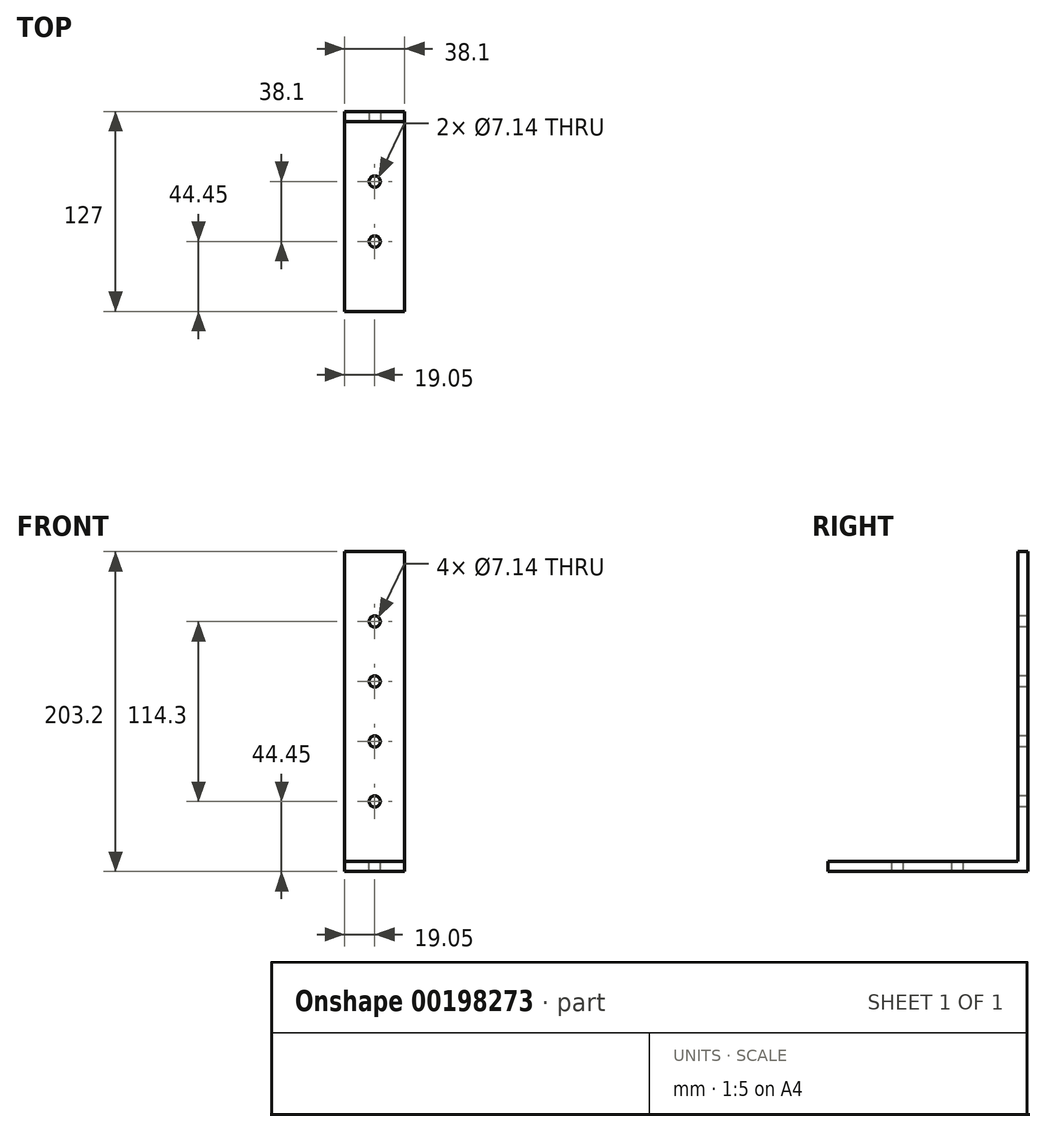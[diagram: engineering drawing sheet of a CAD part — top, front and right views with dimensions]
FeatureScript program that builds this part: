
annotation { "Feature Type Name" : "Feature", "Feature Type Description" : "" }
export const myFeature = defineFeature(function(context is Context, id is Id, definition is map)
    precondition{}
    {
        {
            var Q0;
            Q0=qCreatedBy(makeId("Right.planeOp"),FACE);
            var sketch = newSketch(context, id + "F0", { "sketchPlane" : qUnion([Q0])});
            skLineSegment(sketch, "E0", {"start": v(0, 203.2) * mm, "end": v(0, 0) * mm});
            skLineSegment(sketch, "E1", {"start": v(0, 0) * mm, "end": v(-127, 0) * mm});
            skLineSegment(sketch, "E2.0", {"start": v(-6.35, 6.35) * mm, "end": v(-127, 6.35) * mm});
            skLineSegment(sketch, "E2.1", {"start": v(-6.35, 203.2) * mm, "end": v(-6.35, 6.35) * mm});
            skLineSegment(sketch, "E3", {"start": v(-127, 6.35) * mm, "end": v(-127, 0) * mm});
            skLineSegment(sketch, "E4", {"start": v(-6.35, 203.2) * mm, "end": v(0, 203.2) * mm});
            skSolve(sketch);
        }
        {
            var Q0;
            Q0 = qSketchRegion(id + "F0", true);
            extrude(context, id + "F1", {"entities" : qUnion([Q0]), "endBound" : BoundingType.SYMMETRIC, "depth" : 38.1 * mm, "offsetDistance" : 25.4 * mm});
        }
        {
            var Q0;
            Q0=makeQuery(id+"F1.opExtrude","SWEPT_FACE",FACE,{"disambiguationData":[OSD([sQuery(id+"F0.wireOp",EDGE,"E2.0")])]});
            var sketch = newSketch(context, id + "F2", { "sketchPlane" : qUnion([Q0])});
            skPoint(sketch, "E5", {"position": v(0, -82.55) * mm});
            skPoint(sketch, "E6", {"position": v(0, -44.45) * mm});
            skSolve(sketch);
        }
        {
            var Q0;
            Q0=makeQuery(id+"F1.opExtrude","SWEPT_FACE",FACE,{"disambiguationData":[OSD([sQuery(id+"F0.wireOp",EDGE,"E2.1")])]});
            var sketch = newSketch(context, id + "F3", { "sketchPlane" : qUnion([Q0])});
            skPoint(sketch, "E7", {"position": v(0, 44.45) * mm});
            skPoint(sketch, "E8.0.1.0", {"position": v(0, 82.55) * mm});
            skPoint(sketch, "E8.0.2.0", {"position": v(0, 120.65) * mm});
            skPoint(sketch, "E8.0.3.0", {"position": v(0, 158.75) * mm});
            skLineSegment(sketch, "E8.direction1", {"start": v(0, 44.45) * mm, "end": v(25.4, 44.45) * mm, "construction": true});
            skLineSegment(sketch, "E8.direction2", {"start": v(0, 44.45) * mm, "end": v(0, 82.55) * mm, "construction": true});
            skSolve(sketch);
        }
        {
            var Q0;
            Q0=sQuery(id+"F3.wireOp",VERTEX,"E8.0.3.0");
            var Q1;
            Q1=sQuery(id+"F3.wireOp",VERTEX,"E8.0.2.0");
            var Q2;
            Q2=sQuery(id+"F3.wireOp",VERTEX,"E8.0.1.0");
            var Q3;
            Q3=sQuery(id+"F3.wireOp",VERTEX,"E8.direction1.start");
            var Q4;
            Q4=sQuery(id+"F2.wireOp",VERTEX,"E6");
            var Q5;
            Q5=sQuery(id+"F2.wireOp",VERTEX,"E5");
            var Q6;
            Q6=makeQuery(id+"F1.opExtrude","SWEPT_BODY",BODY,{"disambiguationData":[OSD([sQuery(id+"F0.wireOp",EDGE,"E0"),sQuery(id+"F0.wireOp",EDGE,"E1"),sQuery(id+"F0.wireOp",EDGE,"E2.0"),sQuery(id+"F0.wireOp",EDGE,"E2.1"),sQuery(id+"F0.wireOp",EDGE,"E3"),sQuery(id+"F0.wireOp",EDGE,"E4")])]});
            hole(context, id + "F4", {"style" : HoleStyle.SIMPLE, "endStyle" : HoleEndStyle.THROUGH, "standardTappedOrClearance" : lookupTablePath({ "standard" : "ANSI", "fit" : "Normal (ASME)", "size" : "1/4", "type" : "Clearance" }), "standardBlindInLast" : lookupTablePath({ "fit" : "Normal", "standard" : "ANSI", "engagement" : "75%", "pitch" : "20 tpi", "size" : "1/4", "type" : "Clearance & tapped" }), "holeDiameter" : 7.14 * mm, "majorDiameter" : 6.35 * mm, "isTappedThrough" : true, "tappedDepth" : 12.7 * mm, "tapClearance" : 3, "locations" : qUnion([Q0, Q1, Q2, Q3, Q4, Q5]), "scope" : qUnion([Q6])});
        }
    });
